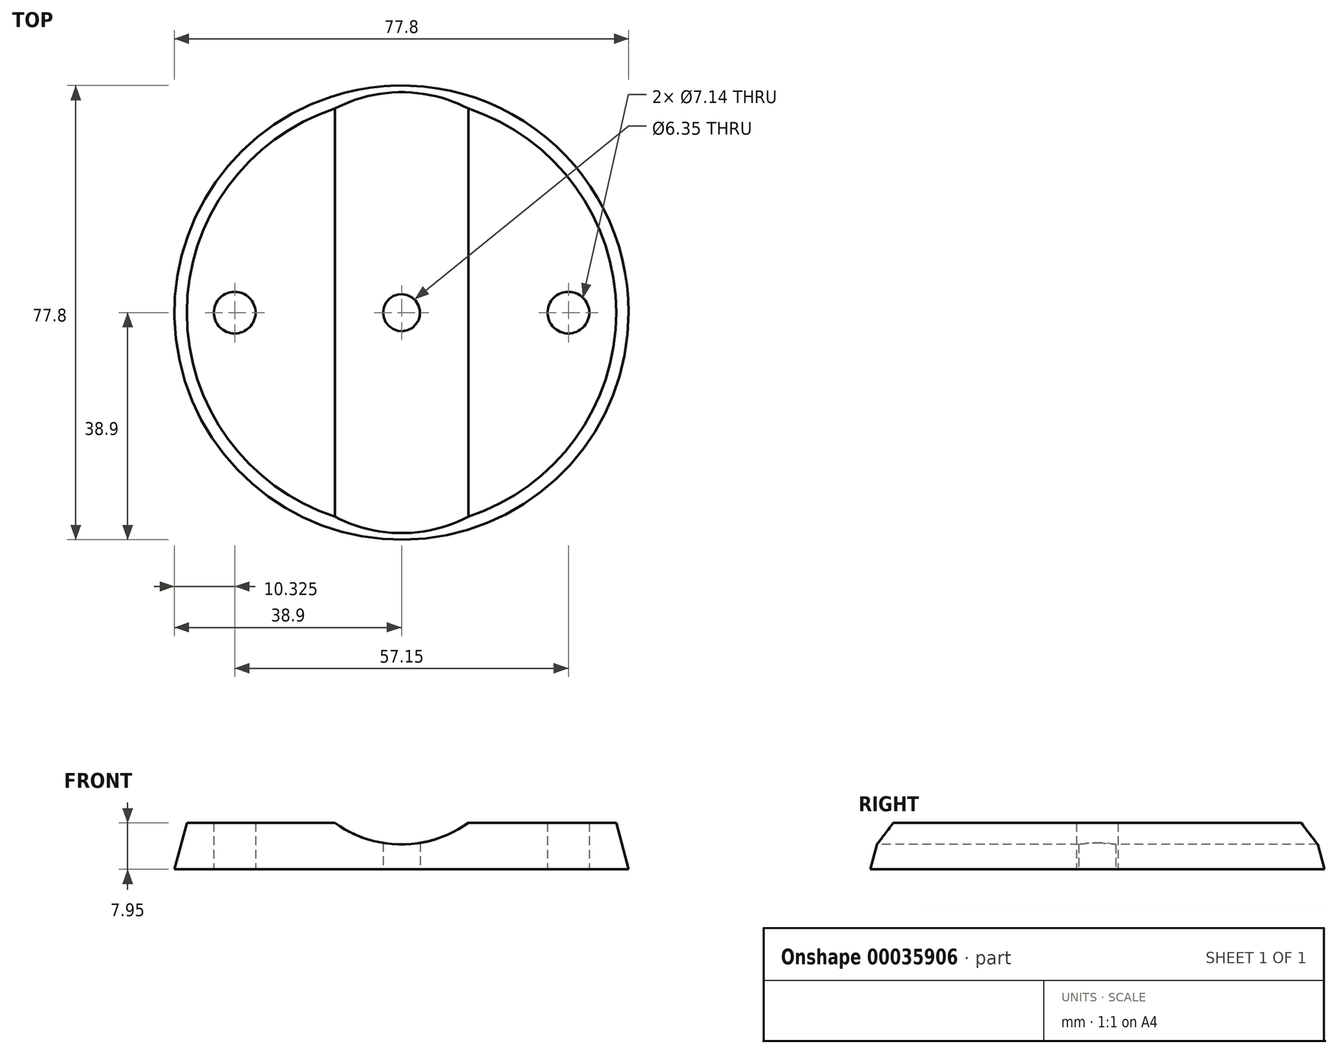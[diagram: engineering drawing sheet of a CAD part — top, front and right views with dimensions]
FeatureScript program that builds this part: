
annotation { "Feature Type Name" : "Feature", "Feature Type Description" : "" }
export const myFeature = defineFeature(function(context is Context, id is Id, definition is map)
    precondition{}
    {
        {
            var Q0;
            Q0=qCreatedBy(makeId("Front.planeOp"),FACE);
            var sketch = newSketch(context, id + "F0", { "sketchPlane" : qUnion([Q0])});
            skLineSegment(sketch, "E0", {"start": v(0, 7.95) * mm, "end": v(0, 0) * mm});
            skLineSegment(sketch, "E1", {"start": v(0, 0) * mm, "end": v(38.9, 0) * mm});
            skLineSegment(sketch, "E2", {"start": v(38.9, 0) * mm, "end": v(36.77, 7.95) * mm});
            skLineSegment(sketch, "E3", {"start": v(36.77, 7.95) * mm, "end": v(0, 7.95) * mm});
            skSolve(sketch);
        }
        {
            var Q0;
            Q0=makeQuery(id+"F0.imprint","IMPRINT",FACE,{"disambiguationData":[TD([[makeQuery(id+"F0.imprint","IMPRINT",EDGE,{"derivedFrom":sQuery(id+"F0.wireOp",EDGE,"E0")}),1.0]])]});
            var Q1;
            Q1=sQuery(id+"F0.wireOp",EDGE,"E0");
            revolve(context, id + "F1", {"entities" : qUnion([Q0]), "axis" : qUnion([Q1]), "revolveType" : RevolveType.FULL});
        }
        {
            var Q0;
            Q0=qCreatedBy(makeId("Front.planeOp"),FACE);
            var sketch = newSketch(context, id + "F2", { "sketchPlane" : qUnion([Q0])});
            skLineSegment(sketch, "E4.0", {"start": v(-36.77, 7.95) * mm, "end": v(36.77, 7.95) * mm});
            skArc(sketch, "E5", {"start": v(-11.42, 7.95) * mm, "mid": v(0, 4.27) * mm, "end": v(11.42, 7.95) * mm});
            skSolve(sketch);
        }
        {
            var Q0;
            Q0 = qSketchRegion(id + "F2", true);
            extrude(context, id + "F3", {"entities" : qUnion([Q0]), "operationType" : NewBodyOperationType.REMOVE, "endBound" : BoundingType.THROUGH_ALL, "oppositeDirection" : true, "depth" : 25.4 * mm, "hasSecondDirection" : true, "secondDirectionBound" : BoundingType.THROUGH_ALL, "secondDirectionOppositeDirection" : false, "secondDirectionDepth" : 25.4 * mm});
        }
        {
            var Q0;
            Q0=makeQuery(id+"F1.opRevolve","SWEPT_FACE",FACE,{"disambiguationData":[OSD([sQuery(id+"F0.wireOp",EDGE,"E1")])]});
            var sketch = newSketch(context, id + "F4", { "sketchPlane" : qUnion([Q0])});
            skLineSegment(sketch, "E6", {"start": v(-28.58, 0) * mm, "end": v(28.58, 0) * mm, "construction": true});
            skCircle(sketch, "E7", {"center": v(0, 0) * mm, "radius": 3.18 * mm});
            skCircle(sketch, "E8", {"center": v(-28.58, 0) * mm, "radius": 3.57 * mm});
            skCircle(sketch, "E9", {"center": v(28.58, 0) * mm, "radius": 3.57 * mm});
            skSolve(sketch);
        }
        {
            var Q0;
            Q0 = qSketchRegion(id + "F4", true);
            extrude(context, id + "F5", {"entities" : qUnion([Q0]), "operationType" : NewBodyOperationType.REMOVE, "endBound" : BoundingType.THROUGH_ALL, "oppositeDirection" : true, "depth" : 25.4 * mm});
        }
    });
